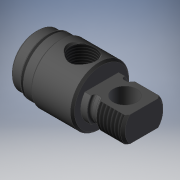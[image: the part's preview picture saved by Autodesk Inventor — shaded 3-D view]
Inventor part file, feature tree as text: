
AUTODESK INVENTOR PART (.ipt)
format: ipt  version: 2019 (Build 230136000, 136)  size: 331,264 bytes
history: native  units: in
note: dims shown in document units (in); Inventor stores cm internally (conversion verified against a paired STEP export)
features: other x168, sketch x7, revolve x4, thread x2, extrude x2, hole x1
ambient origin geometry x8: Origin, YZ Plane, XZ Plane, XY Plane, X Axis, Y Axis, Z Axis, Center Point
bodies: Solid1 (feature_tree)
feature tree (184):
  revolve  "Revolution1"  Angle=360.0deg
  revolve  "Revolution2"  [1 undecoded]
  thread  "Thread1"  [1 undecoded]
  extrude  "Extrusion1"  TaperAngle=360.0deg  [1 undecoded]
  hole  "Hole1"  [1 undecoded]
  revolve  "Revolution3"  [1 undecoded]
  thread  "Thread2"  [1 undecoded]
  revolve  "Revolution4"  [1 undecoded]
  extrude  "Extrusion2"  [1 undecoded]
  other  "1_XY"
  other  "1_YZ"
  other  "1_ZX"
  other  "1_X"
  other  "1_Y"
  other  "1_Z"
  other  "1_Center"
  other  "c1_XY"
  other  "c1_YZ"
  other  "c1_ZX"
  other  "c1_X"
  other  "c1_Y"
  other  "c1_Z"
  other  "c1_Center"
  other  "c2_XY"
  other  "c2_YZ"
  other  "c2_ZX"
  other  "c2_X"
  other  "c2_Y"
  other  "c2_Z"
  other  "c2_Center"
  other  "cc1_XY"
  other  "cc1_YZ"
  other  "cc1_ZX"
  other  "cc1_X"
  other  "cc1_Y"
  other  "cc1_Z"
  other  "cc1_Center"
  other  "cc2_XY"
  other  "cc2_YZ"
  other  "cc2_ZX"
  other  "cc2_X"
  other  "cc2_Y"
  other  "cc2_Z"
  other  "cc2_Center"
  other  "lovra1_XY"
  other  "lovra1_YZ"
  other  "lovra1_ZX"
  other  "lovra1_X"
  other  "lovra1_Y"
  other  "lovra1_Z"
  other  "lovra1_Center"
  other  "lovra2_XY"
  other  "lovra2_YZ"
  other  "lovra2_ZX"
  other  "lovra2_X"
  other  "lovra2_Y"
  other  "lovra2_Z"
  other  "lovra2_Center"
  other  "lovra21_XY"
  other  "lovra21_YZ"
  other  "lovra21_ZX"
  other  "lovra21_X"
  other  "lovra21_Y"
  other  "lovra21_Z"
  other  "lovra21_Center"
  other  "lovra22_XY"
  other  "lovra22_YZ"
  other  "lovra22_ZX"
  other  "lovra22_X"
  other  "lovra22_Y"
  other  "lovra22_Z"
  other  "lovra22_Center"
  other  "lovra3_XY"
  other  "lovra3_YZ"
  other  "lovra3_ZX"
  other  "lovra3_X"
  other  "lovra3_Y"
  other  "lovra3_Z"
  other  "lovra3_Center"
  other  "olen_XY"
  other  "olen_YZ"
  other  "olen_ZX"
  other  "olen_X"
  other  "olen_Y"
  other  "olen_Z"
  other  "olen_Center"
  other  "p1_XY"
  other  "p1_YZ"
  other  "p1_ZX"
  other  "p1_X"
  other  "p1_Y"
  other  "p1_Z"
  other  "p1_Center"
  other  "p2_XY"
  other  "p2_YZ"
  other  "p2_ZX"
  other  "p2_X"
  other  "p2_Y"
  other  "p2_Z"
  other  "p2_Center"
  other  "port_XY"
  other  "port_YZ"
  other  "port_ZX"
  other  "port_X"
  other  "port_Y"
  other  "port_Z"
  other  "port_Center"
  other  "port2_XY"
  other  "port2_YZ"
  other  "port2_ZX"
  other  "port2_X"
  other  "port2_Y"
  other  "port2_Z"
  other  "port2_Center"
  other  "thd1_XY"
  other  "thd1_YZ"
  other  "thd1_ZX"
  other  "thd1_X"
  other  "thd1_Y"
  other  "thd1_Z"
  other  "thd1_Center"
  other  "thd2_XY"
  other  "thd2_YZ"
  other  "thd2_ZX"
  other  "thd2_X"
  other  "thd2_Y"
  other  "thd2_Z"
  other  "thd2_Center"
  other  "to_mounting_bracket_XY"
  other  "to_mounting_bracket_YZ"
  other  "to_mounting_bracket_ZX"
  other  "to_mounting_bracket_X"
  other  "to_mounting_bracket_Y"
  other  "to_mounting_bracket_Z"
  other  "to_mounting_bracket_Center"
  other  "to_nut_XY"
  other  "to_nut_YZ"
  other  "to_nut_ZX"
  other  "to_nut_X"
  other  "to_nut_Y"
  other  "to_nut_Z"
  other  "to_nut_Center"
  other  "to_pin_XY"
  other  "to_pin_YZ"
  other  "to_pin_ZX"
  other  "to_pin_X"
  other  "to_pin_Y"
  other  "to_pin_Z"
  other  "to_pin_Center"
  other  "to_pin_1_XY"
  other  "to_pin_1_YZ"
  other  "to_pin_1_ZX"
  other  "to_pin_1_X"
  other  "to_pin_1_Y"
  other  "to_pin_1_Z"
  other  "to_pin_1_Center"
  other  "to_pin_r_XY"
  other  "to_pin_r_YZ"
  other  "to_pin_r_ZX"
  other  "to_pin_r_X"
  other  "to_pin_r_Y"
  other  "to_pin_r_Z"
  other  "to_pin_r_Center"
  other  "to_screw_XY"
  other  "to_screw_YZ"
  other  "to_screw_ZX"
  other  "to_screw_X"
  other  "to_screw_Y"
  other  "to_screw_Z"
  other  "to_screw_Center"
  other  "to_tube_XY"
  other  "to_tube_YZ"
  other  "to_tube_ZX"
  other  "to_tube_X"
  other  "to_tube_Y"
  other  "to_tube_Z"
  other  "to_tube_Center"
  sketch  "Sketch_8"  dims[d2=0.3547in d3=0.0in d4=0.625in d5=0.0in]
  sketch  "Sketch_15"  dims[d6=0.312in d7=0.75in d8=0.375in d9=0.25in d10=0.5635in d11=0.9284in d12=120.0deg d13=360.0deg]
  sketch  "Sketch_70"
  sketch  "Sketch4"  dims[d0=360.0deg d1=360.0deg]
  sketch  "Sketch_47"  dims[d19=0.0in d20=0.0in d21=0.0in d22=0.0in d23=0.0in d24=0.0in d25=0.0in d26=0.0in]
  sketch  "Sketch_24"  dims[d14=0.2771in d15=0.0in d16=360.0deg]
  sketch  "Sketch_43"  dims[d17=0.5587in d18=0.0in]
note: 8 required parameter values undecoded (feature->parameter linkage not recoverable at this tier; creation-order binding heuristic only, values carry confidence <= 0.55)